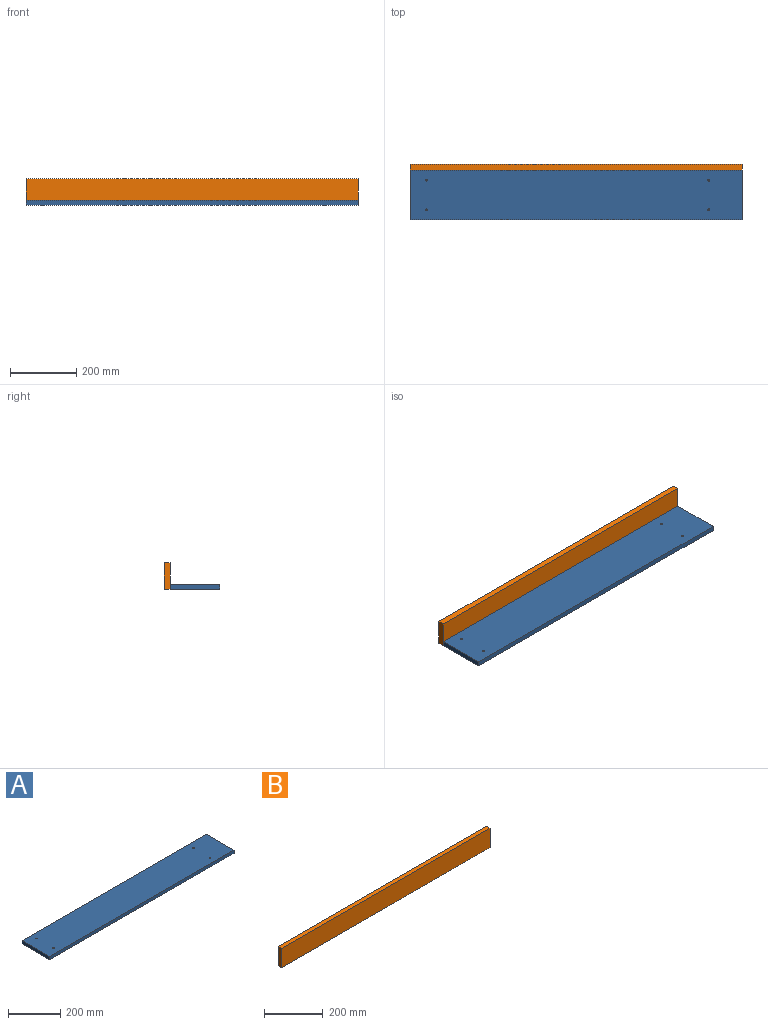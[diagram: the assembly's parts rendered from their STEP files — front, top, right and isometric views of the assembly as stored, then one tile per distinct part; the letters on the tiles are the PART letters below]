
ASSEMBLY  parts=2 mates=1
PART A: 10 faces, bbox 1000x150x15 mm
  f0: plane 1000x15mm, normal (0,1,0), area 15000mm2, adj f1,f3,f4,f5
  f1: plane 150x15mm, normal (-1,0,0), area 2250mm2, adj f0,f2,f4,f5
  f2: plane 1000x15mm, normal (0,-1,0), area 15000mm2, adj f1,f3,f4,f5
  f3: plane 150x15mm, normal (1,0,0), area 2250mm2, adj f0,f2,f4,f5
  f4: plane 1000x150mm, normal (0,0,1), area 149886.9mm2, adj f0,f1,f2,f3,f6,f7,f8,f9
  f5: plane 1000x150mm, normal (0,0,-1), area 149886.9mm2, adj f0,f1,f2,f3,f6,f7,f8,f9
  f6: cylinder r=3mm len=15mm, axis (0,0,1), area 282.7mm2, adj f4,f5
  f7: cylinder r=3mm len=15mm, axis (0,0,1), area 282.7mm2, adj f4,f5
  f8: cylinder r=3mm len=15mm, axis (0,0,1), area 282.7mm2, adj f4,f5
  f9: cylinder r=3mm len=15mm, axis (0,0,1), area 282.7mm2, adj f4,f5
PART B: 6 faces, bbox 1000x18x80 mm
  f0: plane 1000x18mm, normal (0,0,1), area 18000mm2, adj f1,f3,f4,f5
  f1: plane 80x18mm, normal (-1,0,0), area 1440mm2, adj f0,f2,f4,f5
  f2: plane 1000x18mm, normal (0,0,-1), area 18000mm2, adj f1,f3,f4,f5
  f3: plane 80x18mm, normal (1,0,0), area 1440mm2, adj f0,f2,f4,f5
  f4: plane 1000x80mm, normal (0,-1,0), area 80000mm2, adj f0,f1,f2,f3
  f5: plane 1000x80mm, normal (0,1,0), area 80000mm2, adj f0,f1,f2,f3
PLACE A t=(-341.93,115.18,-40.59)mm
PLACE B t=(-341.93,283.18,-40.59)mm
MATE fastened B.f3 <-> A.f3  axis (1,0,0) through (658.07,265.18,-40.59)mm
